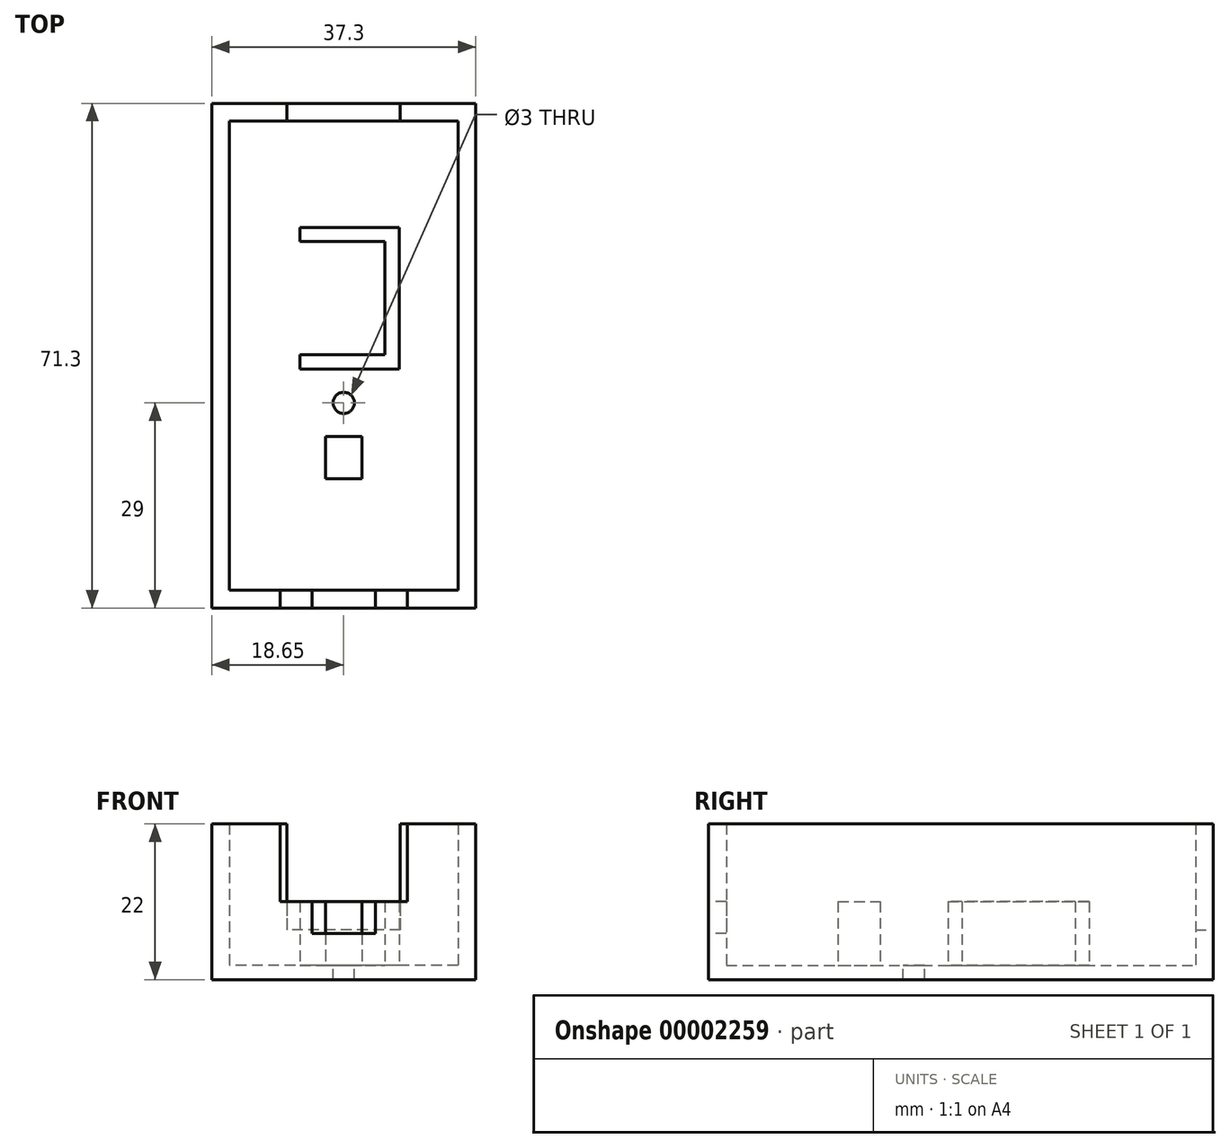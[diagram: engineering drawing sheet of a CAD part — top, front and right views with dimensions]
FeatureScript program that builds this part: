
annotation { "Feature Type Name" : "Feature", "Feature Type Description" : "" }
export const myFeature = defineFeature(function(context is Context, id is Id, definition is map)
    precondition{}
    {
        {
            var Q0;
            Q0=qCreatedBy(makeId("Top.planeOp"),FACE);
            var sketch = newSketch(context, id + "F0", { "sketchPlane" : qUnion([Q0])});
            skLineSegment(sketch, "E0.bottom", {"start": v(16.15, -33.15) * mm, "end": v(-16.15, -33.15) * mm});
            skLineSegment(sketch, "E0.top", {"start": v(16.15, 33.15) * mm, "end": v(-16.15, 33.15) * mm});
            skLineSegment(sketch, "E0.left", {"start": v(16.15, -33.15) * mm, "end": v(16.15, 33.15) * mm});
            skLineSegment(sketch, "E0.right", {"start": v(-16.15, -33.15) * mm, "end": v(-16.15, 33.15) * mm});
            skPoint(sketch, "E0.middle", {"position": v(0, 0) * mm});
            skLineSegment(sketch, "E1.bottom", {"start": v(18.65, -35.65) * mm, "end": v(-18.65, -35.65) * mm});
            skLineSegment(sketch, "E1.top", {"start": v(18.65, 35.65) * mm, "end": v(-18.65, 35.65) * mm});
            skLineSegment(sketch, "E1.left", {"start": v(18.65, -35.65) * mm, "end": v(18.65, 35.65) * mm});
            skLineSegment(sketch, "E1.right", {"start": v(-18.65, -35.65) * mm, "end": v(-18.65, 35.65) * mm});
            skLineSegment(sketch, "E2", {"start": v(0, 35.65) * mm, "end": v(0, -35.65) * mm, "construction": true});
            skLineSegment(sketch, "E3", {"start": v(9, -33.15) * mm, "end": v(9, -35.65) * mm});
            skLineSegment(sketch, "E4", {"start": v(-9, -33.15) * mm, "end": v(-9, -35.65) * mm});
            skLineSegment(sketch, "E5", {"start": v(4.5, -33.15) * mm, "end": v(4.5, -35.65) * mm});
            skLineSegment(sketch, "E6", {"start": v(-4.5, -33.15) * mm, "end": v(-4.5, -35.65) * mm});
            skLineSegment(sketch, "E7", {"start": v(8, 33.15) * mm, "end": v(8, 35.65) * mm});
            skLineSegment(sketch, "E8", {"start": v(-8, 35.65) * mm, "end": v(-8, 33.15) * mm});
            skCircle(sketch, "E9", {"center": v(0, -6.65) * mm, "radius": 1.5 * mm});
            skLineSegment(sketch, "E10.bottom", {"start": v(-2.58, -17.37) * mm, "end": v(2.58, -17.37) * mm});
            skLineSegment(sketch, "E10.top", {"start": v(-2.58, -11.39) * mm, "end": v(2.58, -11.39) * mm});
            skLineSegment(sketch, "E10.left", {"start": v(-2.58, -17.37) * mm, "end": v(-2.58, -11.39) * mm});
            skLineSegment(sketch, "E10.right", {"start": v(2.58, -17.37) * mm, "end": v(2.58, -11.39) * mm});
            skPoint(sketch, "E10.middle", {"position": v(0, -14.38) * mm});
            skLineSegment(sketch, "E11.MirrorCS", {"start": v(-6.18, 0.15) * mm, "end": v(-6.18, -1.85) * mm});
            skLineSegment(sketch, "E12.MirrorCS", {"start": v(-6.18, 18.15) * mm, "end": v(-6.18, 16.15) * mm});
            skLineSegment(sketch, "E13.MirrorCS", {"start": v(-6.18, 16.15) * mm, "end": v(5.82, 16.15) * mm});
            skLineSegment(sketch, "E14.MirrorCS", {"start": v(5.82, 0.15) * mm, "end": v(-6.18, 0.15) * mm});
            skLineSegment(sketch, "E15.MirrorCS", {"start": v(7.82, 18.15) * mm, "end": v(-6.18, 18.15) * mm});
            skLineSegment(sketch, "E16.MirrorCS", {"start": v(5.82, 16.15) * mm, "end": v(5.82, 0.15) * mm});
            skLineSegment(sketch, "E17.MirrorCS", {"start": v(7.82, -1.85) * mm, "end": v(7.82, 18.15) * mm});
            skLineSegment(sketch, "E18.MirrorCS", {"start": v(-6.18, -1.85) * mm, "end": v(7.82, -1.85) * mm});
            skSolve(sketch);
        }
        {
            var Q0;
            {var subQ3=sQuery(id+"F0.wireOp",EDGE,"E0.right");Q0=makeQuery(id+"F0.imprint","IMPRINT",FACE,{"disambiguationData":[TD([[makeQuery(id+"F0.imprint","IMPRINT",EDGE,{"derivedFrom":subQ3}),1.0]])]});}
            var Q1;
            {var subQ3=sQuery(id+"F0.wireOp",EDGE,"E0.left");Q1=makeQuery(id+"F0.imprint","IMPRINT",FACE,{"disambiguationData":[TD([[makeQuery(id+"F0.imprint","IMPRINT",EDGE,{"derivedFrom":subQ3}),-1.0]])]});}
            extrude(context, id + "F1", {"entities" : qUnion([Q0, Q1]), "depth" : 20 * mm});
        }
        {
            var Q0;
            {var subQ3=sQuery(id+"F0.wireOp",EDGE,"E0.right");Q0=makeQuery(id+"F0.imprint","IMPRINT",FACE,{"disambiguationData":[TD([[makeQuery(id+"F0.imprint","IMPRINT",EDGE,{"derivedFrom":subQ3}),1.0]])]});}
            var Q1;
            {var subQ6=sQuery(id+"F0.wireOp",EDGE,"E0.left");Q1=makeQuery(id+"F0.imprint","IMPRINT",FACE,{"disambiguationData":[TD([[makeQuery(id+"F0.imprint","IMPRINT",EDGE,{"derivedFrom":subQ6}),1.0]])]});}
            var Q2;
            {var subQ3=sQuery(id+"F0.wireOp",EDGE,"E0.left");Q2=makeQuery(id+"F0.imprint","IMPRINT",FACE,{"disambiguationData":[TD([[makeQuery(id+"F0.imprint","IMPRINT",EDGE,{"derivedFrom":subQ3}),-1.0]])]});}
            var Q3;
            {var subQ0=sQuery(id+"F0.wireOp",EDGE,"E7");Q3=makeQuery(id+"F0.imprint","IMPRINT",FACE,{"disambiguationData":[TD([[makeQuery(id+"F0.imprint","IMPRINT",EDGE,{"derivedFrom":subQ0}),1.0]])]});}
            var Q4;
            {var subQ0=sQuery(id+"F0.wireOp",EDGE,"E3");Q4=makeQuery(id+"F0.imprint","IMPRINT",FACE,{"disambiguationData":[TD([[makeQuery(id+"F0.imprint","IMPRINT",EDGE,{"derivedFrom":subQ0}),-1.0]])]});}
            var Q5;
            {var subQ0=sQuery(id+"F0.wireOp",EDGE,"E5");Q5=makeQuery(id+"F0.imprint","IMPRINT",FACE,{"disambiguationData":[TD([[makeQuery(id+"F0.imprint","IMPRINT",EDGE,{"derivedFrom":subQ0}),-1.0]])]});}
            var Q6;
            {var subQ0=sQuery(id+"F0.wireOp",EDGE,"E4");Q6=makeQuery(id+"F0.imprint","IMPRINT",FACE,{"disambiguationData":[TD([[makeQuery(id+"F0.imprint","IMPRINT",EDGE,{"derivedFrom":subQ0}),1.0]])]});}
            var Q7;
            Q7=makeQuery(id+"F0.imprint","IMPRINT",FACE,{"disambiguationData":[TD([[makeQuery(id+"F0.imprint","IMPRINT",EDGE,{"derivedFrom":sQuery(id+"F0.wireOp",EDGE,"E10.bottom")}),1.0]])]});
            var Q8;
            Q8=makeQuery(id+"F0.imprint","IMPRINT",FACE,{"disambiguationData":[TD([[makeQuery(id+"F0.imprint","IMPRINT",EDGE,{"derivedFrom":sQuery(id+"F0.wireOp",EDGE,"ZUE0yUBz-VhEi-cPOc-HjuR-ZoeaO4BQ985R")}),-1.0]])]});
            var Q9;
            Q9=makeQuery(id+"F0.imprint","IMPRINT",FACE,{"disambiguationData":[TD([[makeQuery(id+"F0.imprint","IMPRINT",EDGE,{"derivedFrom":sQuery(id+"F0.wireOp",EDGE,"E11.MirrorCS")}),1.0]])]});
            extrude(context, id + "F2", {"entities" : qUnion([Q0, Q1, Q2, Q3, Q4, Q5, Q6, Q7, Q8, Q9]), "operationType" : NewBodyOperationType.ADD, "oppositeDirection" : true, "depth" : 2 * mm});
        }
        {
            var Q0;
            {var subQ0=sQuery(id+"F0.wireOp",EDGE,"E3");Q0=makeQuery(id+"F0.imprint","IMPRINT",FACE,{"disambiguationData":[TD([[makeQuery(id+"F0.imprint","IMPRINT",EDGE,{"derivedFrom":subQ0}),-1.0]])]});}
            var Q1;
            {var subQ0=sQuery(id+"F0.wireOp",EDGE,"E4");Q1=makeQuery(id+"F0.imprint","IMPRINT",FACE,{"disambiguationData":[TD([[makeQuery(id+"F0.imprint","IMPRINT",EDGE,{"derivedFrom":subQ0}),1.0]])]});}
            var Q2;
            Q2=makeQuery(id+"F0.imprint","IMPRINT",FACE,{"disambiguationData":[TD([[makeQuery(id+"F0.imprint","IMPRINT",EDGE,{"derivedFrom":sQuery(id+"F0.wireOp",EDGE,"E11.MirrorCS")}),1.0]])]});
            var Q3;
            Q3=makeQuery(id+"F0.imprint","IMPRINT",FACE,{"disambiguationData":[TD([[makeQuery(id+"F0.imprint","IMPRINT",EDGE,{"derivedFrom":sQuery(id+"F0.wireOp",EDGE,"E10.bottom")}),1.0]])]});
            extrude(context, id + "F3", {"entities" : qUnion([Q0, Q1, Q2, Q3]), "operationType" : NewBodyOperationType.ADD, "depth" : 9 * mm});
        }
        {
            var Q0;
            {var subQ0=sQuery(id+"F0.wireOp",EDGE,"E5");Q0=makeQuery(id+"F0.imprint","IMPRINT",FACE,{"disambiguationData":[TD([[makeQuery(id+"F0.imprint","IMPRINT",EDGE,{"derivedFrom":subQ0}),-1.0]])]});}
            extrude(context, id + "F4", {"entities" : qUnion([Q0]), "operationType" : NewBodyOperationType.ADD, "depth" : 4.5 * mm});
        }
        {
            var Q0;
            {var subQ0=sQuery(id+"F0.wireOp",EDGE,"E7");Q0=makeQuery(id+"F0.imprint","IMPRINT",FACE,{"disambiguationData":[TD([[makeQuery(id+"F0.imprint","IMPRINT",EDGE,{"derivedFrom":subQ0}),1.0]])]});}
            extrude(context, id + "F5", {"entities" : qUnion([Q0]), "operationType" : NewBodyOperationType.ADD, "depth" : 5 * mm});
        }
        {
            var Q0;
            Q0=makeQuery(id+"F0.imprint","IMPRINT",FACE,{"disambiguationData":[TD([[makeQuery(id+"F0.imprint","IMPRINT",EDGE,{"derivedFrom":sQuery(id+"F0.wireOp",EDGE,"E10.bottom")}),1.0]])]});
            var Q1;
            Q1=makeQuery(id+"F0.imprint","IMPRINT",FACE,{"disambiguationData":[TD([[makeQuery(id+"F0.imprint","IMPRINT",EDGE,{"derivedFrom":sQuery(id+"F0.wireOp",EDGE,"ZUE0yUBz-VhEi-cPOc-HjuR-ZoeaO4BQ985R")}),-1.0]])]});
            extrude(context, id + "F6", {"entities" : qUnion([Q0, Q1]), "operationType" : NewBodyOperationType.ADD, "depth" : 5 * mm, "hasDraft" : true, "draftAngle" : 3 * degree, "draftPullDirection" : true});
        }
    });
